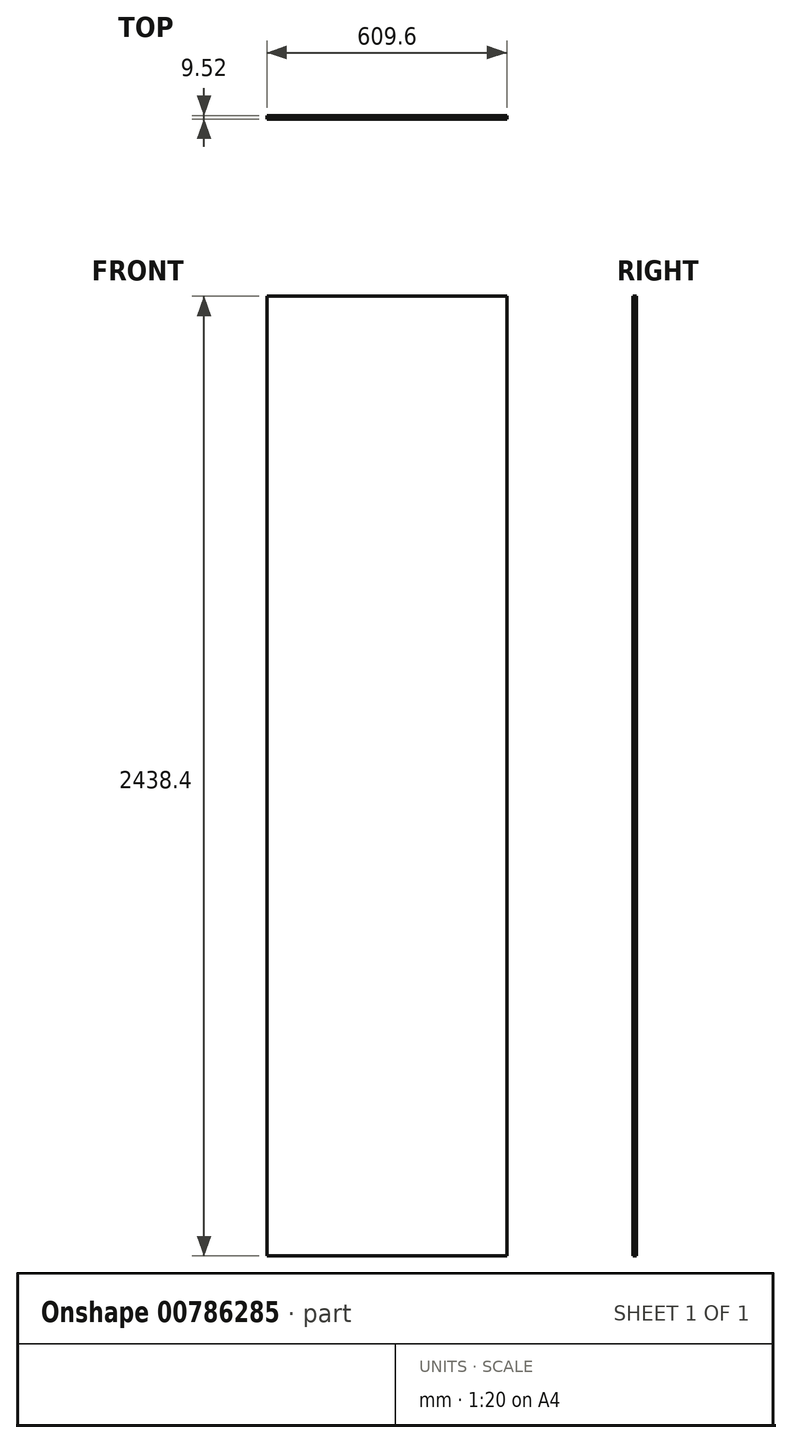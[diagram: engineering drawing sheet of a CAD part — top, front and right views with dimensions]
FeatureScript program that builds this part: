
annotation { "Feature Type Name" : "Feature", "Feature Type Description" : "" }
export const myFeature = defineFeature(function(context is Context, id is Id, definition is map)
    precondition{}
    {
        {
            var Q0;
            Q0=qCreatedBy(makeId("Front.planeOp"),FACE);
            var sketch = newSketch(context, id + "F0", { "sketchPlane" : qUnion([Q0])});
            skLineSegment(sketch, "E0.bottom", {"start": v(-304.8, 1219.2) * mm, "end": v(304.8, 1219.2) * mm});
            skLineSegment(sketch, "E0.top", {"start": v(-304.8, -1219.2) * mm, "end": v(304.8, -1219.2) * mm});
            skLineSegment(sketch, "E0.left", {"start": v(-304.8, 1219.2) * mm, "end": v(-304.8, -1219.2) * mm});
            skLineSegment(sketch, "E0.right", {"start": v(304.8, 1219.2) * mm, "end": v(304.8, -1219.2) * mm});
            skPoint(sketch, "E0.middle", {"position": v(0, 0) * mm});
            skSolve(sketch);
        }
        {
            var Q0;
            Q0=makeQuery(id+"F0.imprint","IMPRINT",FACE,{"disambiguationData":[TD([[makeQuery(id+"F0.imprint","IMPRINT",EDGE,{"derivedFrom":sQuery(id+"F0.wireOp",EDGE,"E0.bottom")}),-1.0]])]});
            extrude(context, id + "F1", {"entities" : qUnion([Q0]), "endBound" : BoundingType.SYMMETRIC, "depth" : 9.52 * mm, "offsetDistance" : 25.4 * mm});
        }
    });
